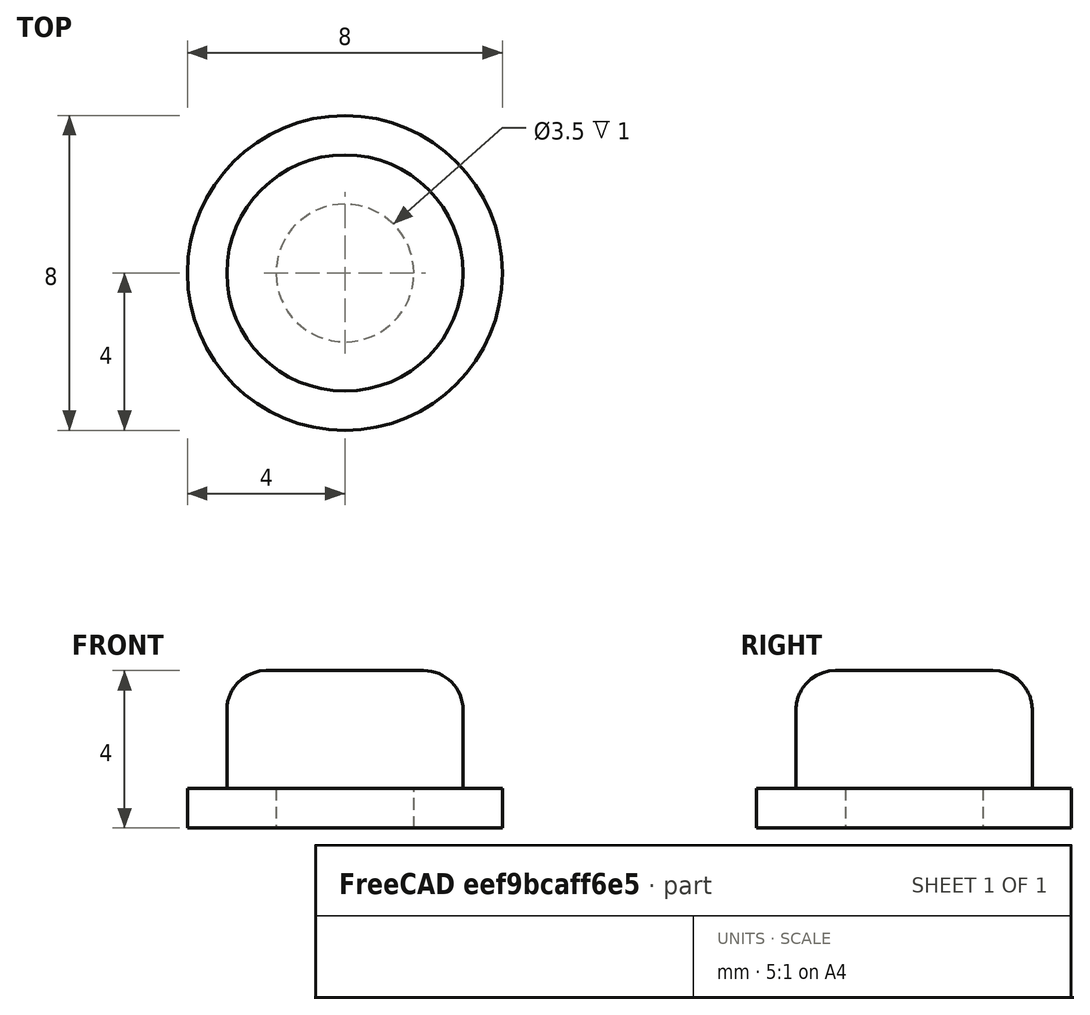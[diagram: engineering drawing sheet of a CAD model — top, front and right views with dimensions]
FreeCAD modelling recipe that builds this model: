
FCSTD DOCUMENT  (FreeCAD 0.17R13541 (Git))
Label: Button
License: All rights reserved
LicenseURL: http://en.wikipedia.org/wiki/All_rights_reserved
objects: Sketcher::SketchObject×3, PartDesign::Pad×2, PartDesign::Fillet×1, PartDesign::Pocket×1, PartDesign::Body×1, Mesh::Feature×1
note: 11 computed .brp shape members not serialized (recipe doc carries the construction recipe); baked Part::Feature solids carry a one-line shape summary decoded from their .brp

FEATURE [Sketcher::SketchObject] Sketch
  MapMode = 5
  Support = -> [XY_Plane]
  sketch-geometry (1):
    g0: Circle CenterX=0 CenterY=0 CenterZ=0 NormalX=0 NormalY=0 NormalZ=1 AngleXU=0 Radius=4
  constraints (2):
    c: Coincident(g0,g-1)
    c: Radius(g0) = 4
FEATURE [PartDesign::Pad] Pad
  Length = 1
  Length2 = 100
  Profile = -> Sketch
  Type = 0
FEATURE [Sketcher::SketchObject] Sketch001
  MapMode = 5
  Placement = pos=(0,0,1) rot=(0,0,1;0rad)
  Support = -> [Pad]
  sketch-geometry (1):
    g0: Circle CenterX=0 CenterY=0 CenterZ=0 NormalX=0 NormalY=0 NormalZ=1 AngleXU=0 Radius=3
  constraints (2):
    c: Coincident(g0,g-1)
    c: Radius(g0) = 3
FEATURE [PartDesign::Pad] Pad001
  BaseFeature = -> Pad
  Length = 3
  Length2 = 100
  Profile = -> Sketch001
  Type = 0
FEATURE [PartDesign::Fillet] Fillet
  Base = -> Pad001 [Edge6]
  BaseFeature = -> Pad001
  Radius = 1
FEATURE [Sketcher::SketchObject] Sketch002
  MapMode = 5
  Placement = pos=(0,0,0) rot=(1,0,0;3.14159rad)
  Support = -> [Fillet]
  sketch-geometry (1):
    g0: Circle CenterX=0 CenterY=0 CenterZ=0 NormalX=0 NormalY=0 NormalZ=1 AngleXU=0 Radius=1.75
  constraints (2):
    c: Coincident(g0,g-1)
    c: Radius(g0) = 1.75
FEATURE [PartDesign::Pocket] Pocket
  BaseFeature = -> Fillet
  Length = 1
  Length2 = 100
  Profile = -> Sketch002
  Type = 0
FEATURE [PartDesign::Body] Body
  Group = -> [Sketch,Pad,Sketch001,Pad001,Fillet,Sketch002,Pocket]
  Origin = -> Origin
  Tip = -> Pocket
FEATURE [Mesh::Feature] Mesh  label="Pocket (Meshed)"
